# Revit family: SE-SU-410_GENERADO
name_source: partatom
category: Equipos especializados
revit_build: Autodesk Revit 2014 (Build: 20130308_1515(x64)
units: mm (PartAtom-declared; Revit-internal decimal feet)

## types (3) — shared parameters
Comentarios de tipo = Tabletop model. 10 m³/h. 420 mm.
Depth = 529 mm  [stored 1.73556 ft]
Fabricante = SAMMIC S.L.
Foodservice Equipment Identifier = Sí
Height = 413 mm  [stored 1.35499 ft]
Revision Code = 1
Specification by Manufacturer = 420 mm. sealing bar.
10 m³/h Busch vacuum pump.
Vacuum controlled by sensor.
URL = https://www.sammic.com
Weight in Pounds = 141.1
Width = 484 mm  [stored 1.58793 ft]

## per-type parameters (varying)
| type | Cycle | FL Amps | Modelo | URL Cutsheet | Volts |
| Vacuum packing machine SE-410  230/50-60/1 | 50 Hz | 3 A | 1140634 | http://www.sammic.com | 230 V |
| Vacuum packing machine SE-410 120/50-60/1 | 60 Hz | 6 A | 1140635 | http://www.sammic.com | 120 V |
| Vacuum packing machine SE-410 230/50-60/1 KSA | 50 Hz | 3 A | 1140648 |  | 230 V |

note: column(s) folded — value = type name in every type: Descripción

note: [stored X ft] marks values corroborated as IEEE doubles in the binary element streams (Revit-internal decimal feet)
